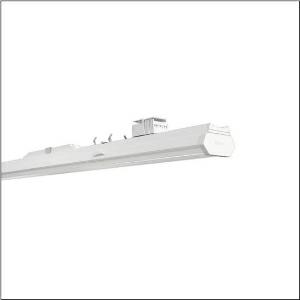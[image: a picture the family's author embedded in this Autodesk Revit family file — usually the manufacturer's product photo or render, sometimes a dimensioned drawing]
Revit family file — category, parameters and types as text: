
# Revit family: licross_r__11_protected_mo_51tp12mn695g_a217
name_source: partatom
category: Lighting Fixtures
units: mm (PartAtom-declared; Revit-internal decimal feet)

## family parameters
Cut with Voids When Loaded = No
Host = Face
Light Source = No
Part Type = Normal
Room Calculation Point = No
Round Connector Dimension = Use Diameter
Shared = No

## types (1)
- --- (1 x LED, 9780 lm, 55.3 W, 6500K)
    Apparent Load = 55 VA
    CIE Flux Codes = 73 92 98 99 100
    Color Rendering = 80
    Color Temperature = 6500K
    Default Elevation = 1800 mm
    Description = Licross® 11 Protected MO, luminaire insert, of sheet steel, galvanised, coil coated, white, length: 1.500mm, width: 90mm, height: 101mm, LED rated luminous flux: 9.780lm, light colour: 865, control gear: ON/OFF Multilumen, with plug, 3-pole, with phase selection, mains connection: 220..240V, AC, 50/60Hz, rated input power: 55W, internal wiring halogen-free, primary light control with lens, of plastic, primary optical cover: cover, of PMMA, light emission: direct distribution, primary light characteristic: symmetric, protection rating (complete): IP64, insulation class (complete): insulation class I (protective earthing), certification: CE, ENEC, VDE, UKCA, protection symbol: D if used in an environment with conductive dust loads with corresponding accessories, impact resistance: IK06, permissible ambient temperature for indoor applications: -35..+40°C, corresponds to IFS (International Featured Standards) requirements for safety and quality in the food industry, reducing of maximum allowable ambient temperature of 5°C with ceiling mounting, LABS conformity tested according to VDMA 24364:2018-05, packaging unit: 1 piece
    Height = 92 mm
    Lamp = 1 x LED
    Lamp Light Flux = 9780 lm
    Lamp Power = 55.3 W
    Lamp count = 1
    Length = 1500 mm
    Luminous efficacy = 177 lm/W
    Manufacturer = Siteco
    ModVariant = No
    Model = 51TP12MN695G
    Mounting Place = Ceiling
    Mounting Type = Pendant
    Number of Poles = 1
    OnlyDefault = Yes
    Power Factor = 1
    Product Name = Licross® 11 Protected MO
    Product group = luminaire insert | ceiling pendant
    ProductGroupID = 902
    Protection Class = Protection class I
    Protection Degree = IP 64
    RLX_Detail_Level = 1
    RLX_Emergency_Light_Flux = 0 lm
    RLX_Emergency_Type = 0
    RLX_Emergency_Type_DB = No
    RlxData = <blob elided: 22145 chars, md5=a9c85091>
    Socket = socket
    Standby Power = 0 W
    System Light Flux = 9780 lm
    System Power = 55 W
    Type Comments = factory setting: luminous flux: 100 % | (A | C | E) | 126 mA
    Type Image = l_1256148.jpg
    URL = http://relux.com
    VarID = @adj_051515
    Voltage = 0 V
    Weight = 0.00 kg
    Width = 88 mm

## geometry (parser evidence)
native form markers: Blend x4, Sweep x11
no freeform markers — native parametric forms only
